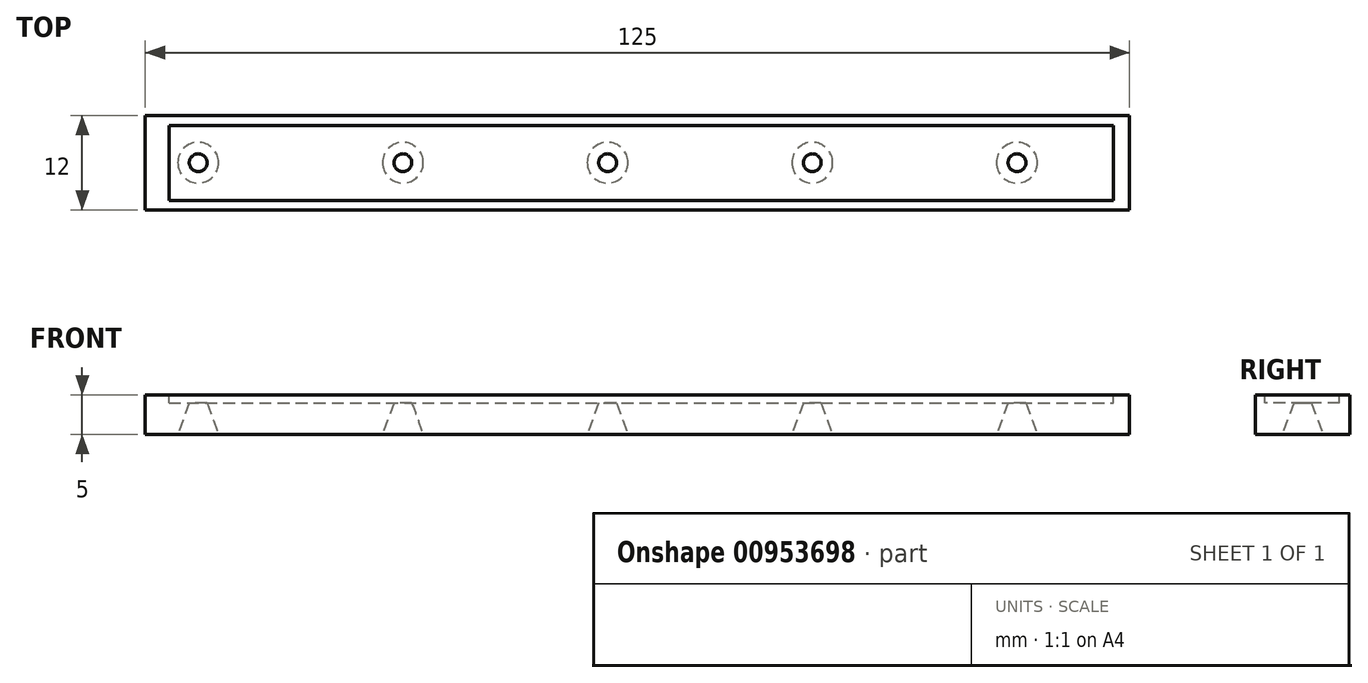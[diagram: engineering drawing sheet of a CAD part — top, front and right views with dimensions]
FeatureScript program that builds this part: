
annotation { "Feature Type Name" : "Feature", "Feature Type Description" : "" }
export const myFeature = defineFeature(function(context is Context, id is Id, definition is map)
    precondition{}
    {
        {
            var Q0;
            Q0=qCreatedBy(makeId("Top.planeOp"),FACE);
            var sketch = newSketch(context, id + "F0", { "sketchPlane" : qUnion([Q0])});
            skLineSegment(sketch, "E0.bottom", {"start": v(0, 0) * mm, "end": v(125, 0) * mm});
            skLineSegment(sketch, "E0.top", {"start": v(0, 12) * mm, "end": v(125, 12) * mm});
            skLineSegment(sketch, "E0.left", {"start": v(0, 0) * mm, "end": v(0, 12) * mm});
            skLineSegment(sketch, "E0.right", {"start": v(125, 0) * mm, "end": v(125, 12) * mm});
            skSolve(sketch);
        }
        {
            var Q0;
            Q0=makeQuery(id+"F0.imprint","IMPRINT",FACE,{"disambiguationData":[TD([[makeQuery(id+"F0.imprint","IMPRINT",EDGE,{"derivedFrom":sQuery(id+"F0.wireOp",EDGE,"E0.bottom")}),1.0]])]});
            extrude(context, id + "F1", {"entities" : qUnion([Q0]), "depth" : 5 * mm, "offsetDistance" : 25 * mm});
        }
        {
            var Q0;
            Q0=makeQuery(id+"F1.opExtrude","CAP_FACE",FACE,{"disambiguationData":[OSD([sQuery(id+"F0.wireOp",EDGE,"E0.bottom"),sQuery(id+"F0.wireOp",EDGE,"E0.top"),sQuery(id+"F0.wireOp",EDGE,"E0.left"),sQuery(id+"F0.wireOp",EDGE,"E0.right")])],"isStart":false});
            var sketch = newSketch(context, id + "F2", { "sketchPlane" : qUnion([Q0])});
            skLineSegment(sketch, "E1.bottom", {"start": v(3, 10.7) * mm, "end": v(123, 10.7) * mm});
            skLineSegment(sketch, "E1.top", {"start": v(3, 1.2) * mm, "end": v(123, 1.2) * mm});
            skLineSegment(sketch, "E1.left", {"start": v(3, 10.7) * mm, "end": v(3, 1.2) * mm});
            skLineSegment(sketch, "E1.right", {"start": v(123, 10.7) * mm, "end": v(123, 1.2) * mm});
            skSolve(sketch);
        }
        {
            var Q0;
            Q0=makeQuery(id+"F2.imprint","IMPRINT",FACE,{"disambiguationData":[TD([[makeQuery(id+"F2.imprint","IMPRINT",EDGE,{"derivedFrom":sQuery(id+"F2.wireOp",EDGE,"E1.bottom")}),-1.0]])]});
            extrude(context, id + "F3", {"entities" : qUnion([Q0]), "operationType" : NewBodyOperationType.REMOVE, "oppositeDirection" : true, "depth" : 1 * mm, "offsetDistance" : 25 * mm});
        }
        {
            var Q0;
            Q0=makeQuery(id+"F1.opExtrude","CAP_FACE",FACE,{"disambiguationData":[OSD([sQuery(id+"F0.wireOp",EDGE,"E0.bottom"),sQuery(id+"F0.wireOp",EDGE,"E0.top"),sQuery(id+"F0.wireOp",EDGE,"E0.left"),sQuery(id+"F0.wireOp",EDGE,"E0.right")])],"isStart":true});
            var sketch = newSketch(context, id + "F4", { "sketchPlane" : qUnion([Q0])});
            skCircle(sketch, "E2", {"center": v(6.72, -6.01) * mm, "radius": 2.59 * mm});
            skCircle(sketch, "E3.1.0.0", {"center": v(32.72, -6.01) * mm, "radius": 2.59 * mm});
            skCircle(sketch, "E3.2.0.0", {"center": v(58.72, -6.01) * mm, "radius": 2.59 * mm});
            skCircle(sketch, "E3.3.0.0", {"center": v(84.72, -6.01) * mm, "radius": 2.59 * mm});
            skCircle(sketch, "E3.4.0.0", {"center": v(110.72, -6.01) * mm, "radius": 2.59 * mm});
            skLineSegment(sketch, "E3.direction1", {"start": v(6.72, -6.01) * mm, "end": v(32.72, -6.01) * mm, "construction": true});
            skSolve(sketch);
        }
        {
            var Q0;
            Q0=makeQuery(id+"F4.imprint","IMPRINT",FACE,{"disambiguationData":[TD([[makeQuery(id+"F4.imprint","IMPRINT",EDGE,{"derivedFrom":sQuery(id+"F4.wireOp",EDGE,"E2")}),1.0]])]});
            var Q1;
            Q1=makeQuery(id+"F4.imprint","IMPRINT",FACE,{"disambiguationData":[TD([[makeQuery(id+"F4.imprint","IMPRINT",EDGE,{"derivedFrom":sQuery(id+"F4.wireOp",EDGE,"E3.1.0.0")}),1.0]])]});
            var Q2;
            Q2=makeQuery(id+"F4.imprint","IMPRINT",FACE,{"disambiguationData":[TD([[makeQuery(id+"F4.imprint","IMPRINT",EDGE,{"derivedFrom":sQuery(id+"F4.wireOp",EDGE,"E3.2.0.0")}),1.0]])]});
            var Q3;
            Q3=makeQuery(id+"F4.imprint","IMPRINT",FACE,{"disambiguationData":[TD([[makeQuery(id+"F4.imprint","IMPRINT",EDGE,{"derivedFrom":sQuery(id+"F4.wireOp",EDGE,"E3.3.0.0")}),1.0]])]});
            var Q4;
            Q4=makeQuery(id+"F4.imprint","IMPRINT",FACE,{"disambiguationData":[TD([[makeQuery(id+"F4.imprint","IMPRINT",EDGE,{"derivedFrom":sQuery(id+"F4.wireOp",EDGE,"E3.4.0.0")}),1.0]])]});
            extrude(context, id + "F5", {"entities" : qUnion([Q0, Q1, Q2, Q3, Q4]), "operationType" : NewBodyOperationType.REMOVE, "oppositeDirection" : true, "depth" : 5 * mm, "offsetDistance" : 25 * mm, "hasDraft" : true, "draftAngle" : 20 * degree, "draftPullDirection" : true});
        }
    });
